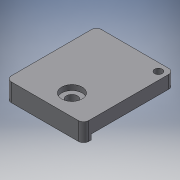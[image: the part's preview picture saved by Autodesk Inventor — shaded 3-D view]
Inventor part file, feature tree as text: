
AUTODESK INVENTOR PART (.ipt)
format: ipt  version: 2019 (Build 230136000, 136)  size: 153,088 bytes
history: native  units: in
note: dims shown in document units (in); Inventor stores cm internally (conversion verified against a paired STEP export)
features: sketch x6, extrude x5, projected_geometry x2, hole x1, fillet x1
ambient origin geometry x8: Origin, YZ Plane, XZ Plane, XY Plane, X Axis, Y Axis, Z Axis, Center Point
bodies: Solid1 (feature_tree)
feature tree (15):
  extrude  "Extrusion1"  Depth=1.1811in
  hole  "Hole1"  [1 undecoded]
  extrude  "Extrusion3"  Depth=0.1181in TaperAngle=0.0deg
  extrude  "Extrusion4"  Depth=0.1969in TaperAngle=0.0deg
  extrude  "Extrusion5"  Depth=0.0787in
  extrude  "Extrusion6"  Depth=0.315in
  fillet  "Fillet1"  Radius=0.0787in
  sketch  "Sketch1"  dims[d0=0.1969in d1=0.0in d2=1.1811in]
  sketch  "Sketch3"  dims[d3=1.5748in]
  projected_geometry  "Projected Loop1"
  sketch  "Sketch4"  dims[d9=0.1695in d10=0.2362in d11=0.279in d12=0.0787in d13=0.5635in d14=0.315in d15=0.8108in d16=0.305in]
  sketch  "Sketch5"  dims[d17=0.6487in d18=0.1181in d19=0.0in]
  sketch  "Sketch6"  dims[d20=0.1181in d23=0.1969in d24=0.0in]
  projected_geometry  "Projected Loop2"
  sketch  "Sketch7"  dims[d28=0.315in d29=0.0787in d30=0.315in d31=0.0787in d32=0.0in d33=0.3937in d34=0.3937in d35=0.1181in d36=0.0787in d37=0.0in]
note: 1 required parameter value undecoded (feature->parameter linkage not recoverable at this tier; creation-order binding heuristic only, values carry confidence <= 0.55)
